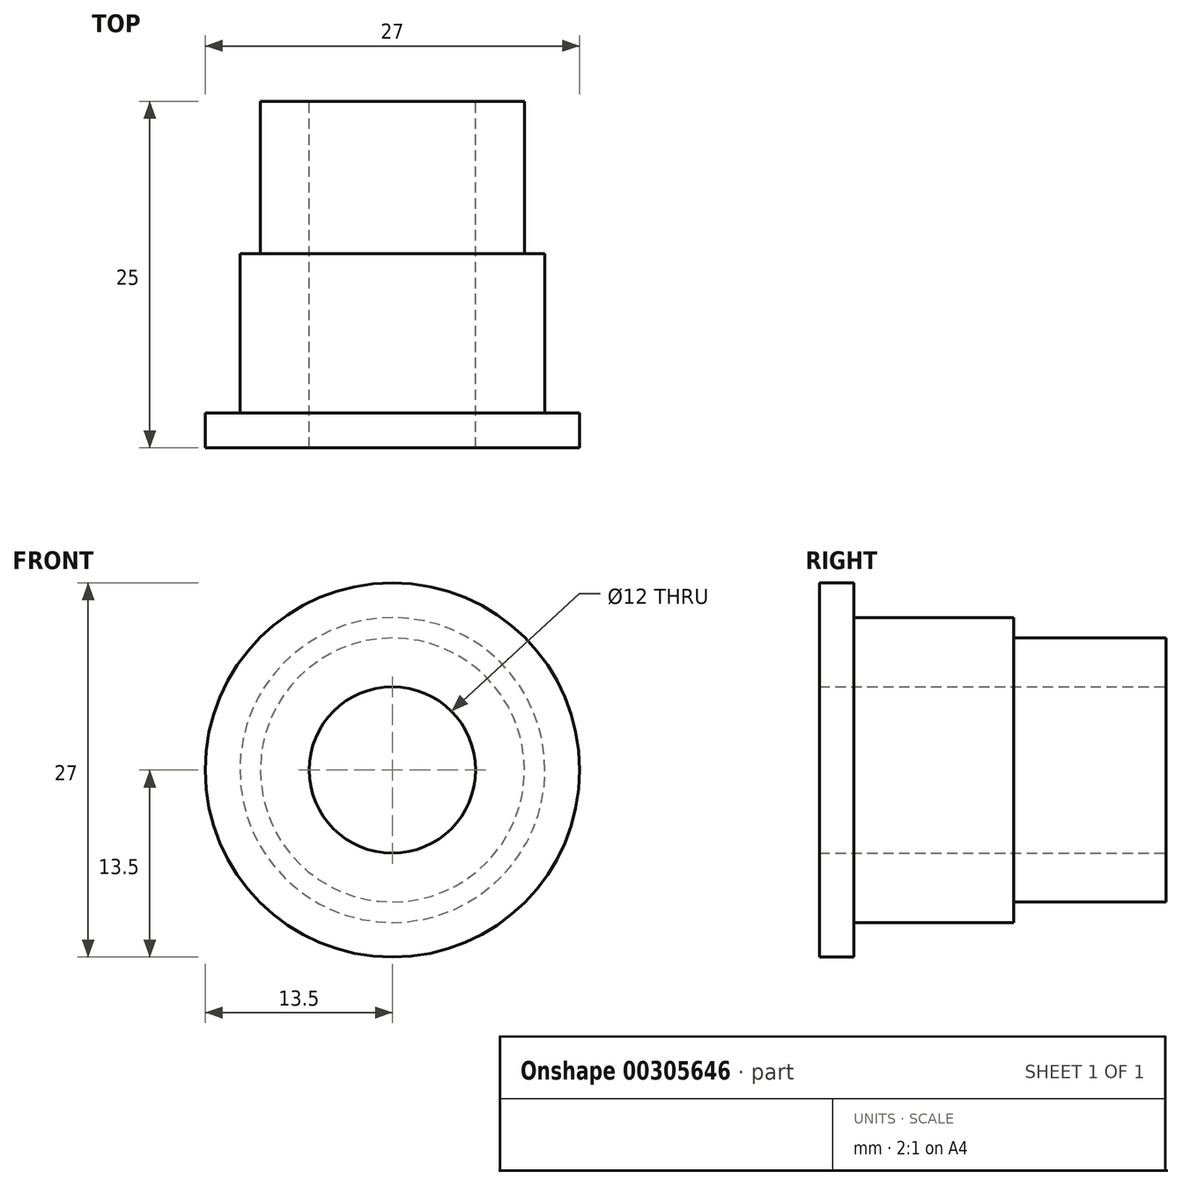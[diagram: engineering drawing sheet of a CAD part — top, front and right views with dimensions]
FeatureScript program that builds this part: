
annotation { "Feature Type Name" : "Feature", "Feature Type Description" : "" }
export const myFeature = defineFeature(function(context is Context, id is Id, definition is map)
    precondition{}
    {
        {
            var Q0;
            Q0=qCreatedBy(makeId("Front.planeOp"),FACE);
            var sketch = newSketch(context, id + "F0", { "sketchPlane" : qUnion([Q0])});
            skCircle(sketch, "E0", {"center": v(0, 0) * mm, "radius": 13.5 * mm});
            skCircle(sketch, "E1", {"center": v(0, 0) * mm, "radius": 11.99 * mm});
            skSolve(sketch);
        }
        {
            var Q0;
            Q0=qSketchRegion(id+"F0",true);
            var Q1;
            Q1=makeQuery(id+"F0.imprint","IMPRINT",FACE,{"disambiguationData":[TD([[makeQuery(id+"F0.imprint","IMPRINT",EDGE,{"derivedFrom":sQuery(id+"F0.wireOp",EDGE,"E1")}),1.0]])]});
            extrude(context, id + "F1", {"entities" : qUnion([Q0, Q1]), "depth" : 2.5 * mm});
        }
        {
            var Q0;
            Q0=makeQuery(id+"F1.opExtrude","CAP_FACE",FACE,{"disambiguationData":[OSD([sQuery(id+"F0.wireOp",EDGE,"E0")])],"isStart":true});
            var sketch = newSketch(context, id + "F2", { "sketchPlane" : qUnion([Q0])});
            skCircle(sketch, "E2", {"center": v(0, 0) * mm, "radius": 11 * mm});
            skSolve(sketch);
        }
        {
            var Q0;
            Q0=qSketchRegion(id+"F2",true);
            extrude(context, id + "F3", {"entities" : qUnion([Q0]), "operationType" : NewBodyOperationType.ADD, "depth" : 11.5 * mm});
        }
        {
            var Q0;
            Q0=makeQuery(id+"F3.opExtrude","CAP_FACE",FACE,{"disambiguationData":[OSD([sQuery(id+"F2.wireOp",EDGE,"E2")])],"isStart":false});
            var sketch = newSketch(context, id + "F4", { "sketchPlane" : qUnion([Q0])});
            skCircle(sketch, "E3", {"center": v(0, 0) * mm, "radius": 9.52 * mm});
            skSolve(sketch);
        }
        {
            var Q0;
            Q0=makeQuery(id+"F4.imprint","IMPRINT",FACE,{"disambiguationData":[TD([[makeQuery(id+"F4.imprint","IMPRINT",EDGE,{"derivedFrom":sQuery(id+"F4.wireOp",EDGE,"E3")}),1.0]])]});
            extrude(context, id + "F5", {"entities" : qUnion([Q0]), "operationType" : NewBodyOperationType.ADD, "depth" : 11 * mm});
        }
        {
            var Q0;
            Q0=makeQuery(id+"F5.opExtrude","CAP_FACE",FACE,{"disambiguationData":[OSD([sQuery(id+"F4.wireOp",EDGE,"E3")])],"isStart":false});
            var sketch = newSketch(context, id + "F6", { "sketchPlane" : qUnion([Q0])});
            skCircle(sketch, "E4", {"center": v(0, 0) * mm, "radius": 6 * mm});
            skSolve(sketch);
        }
        {
            var Q0;
            Q0=makeQuery(id+"F6.imprint","IMPRINT",FACE,{"disambiguationData":[TD([[makeQuery(id+"F6.imprint","IMPRINT",EDGE,{"derivedFrom":sQuery(id+"F6.wireOp",EDGE,"E4")}),1.0]])]});
            extrude(context, id + "F7", {"entities" : qUnion([Q0]), "operationType" : NewBodyOperationType.REMOVE, "oppositeDirection" : true, "depth" : 25 * mm});
        }
    });
